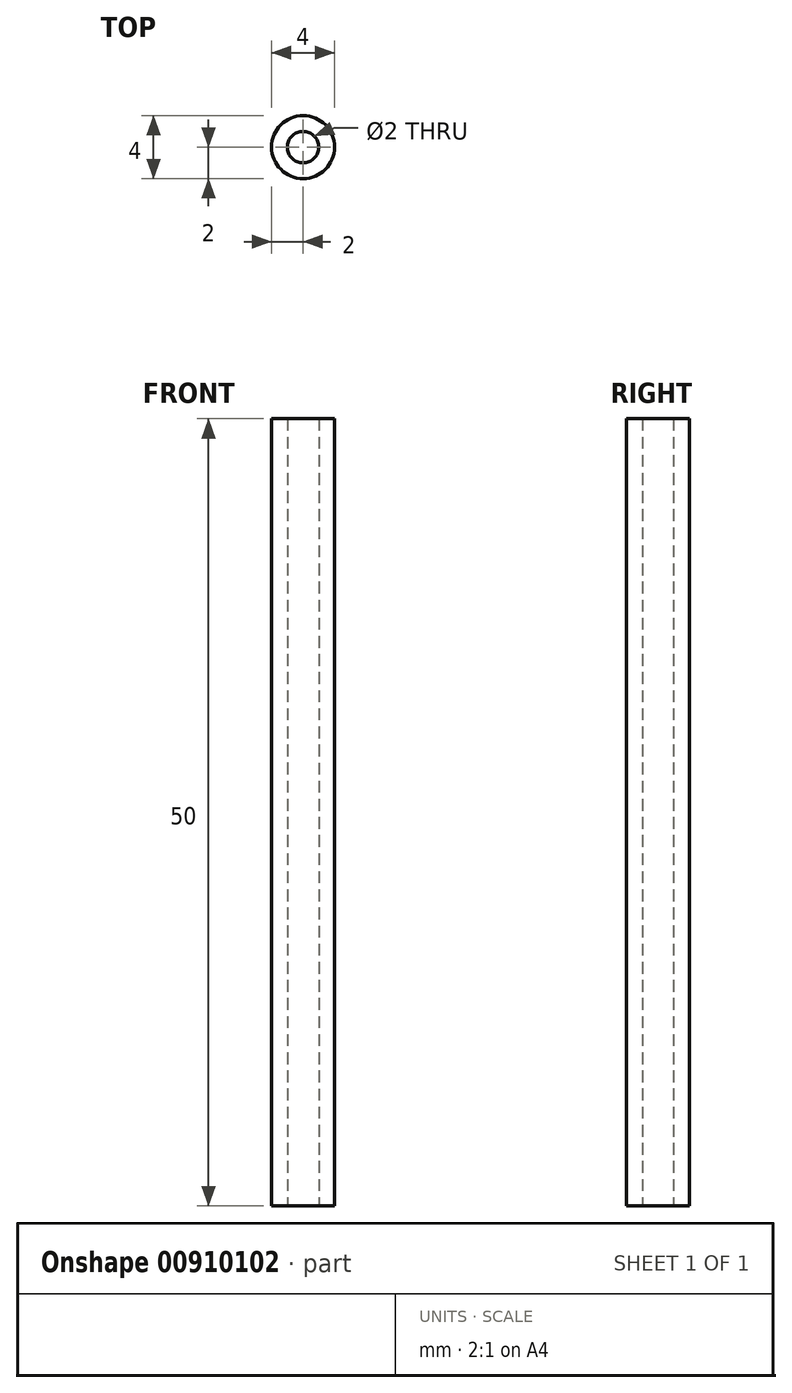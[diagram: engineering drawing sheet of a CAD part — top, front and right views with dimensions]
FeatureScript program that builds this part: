
annotation { "Feature Type Name" : "Feature", "Feature Type Description" : "" }
export const myFeature = defineFeature(function(context is Context, id is Id, definition is map)
    precondition{}
    {
        {
            var Q0;
            Q0=qCreatedBy(makeId("Top.planeOp"),FACE);
            var sketch = newSketch(context, id + "F0", { "sketchPlane" : qUnion([Q0])});
            skCircle(sketch, "E0", {"center": v(0, 0) * mm, "radius": 2 * mm});
            skCircle(sketch, "E1", {"center": v(0, 0) * mm, "radius": 1 * mm});
            skSolve(sketch);
        }
        {
            var Q0;
            Q0=makeQuery(id+"F0.imprint","IMPRINT",FACE,{"disambiguationData":[TD([[makeQuery(id+"F0.imprint","IMPRINT",EDGE,{"derivedFrom":sQuery(id+"F0.wireOp",EDGE,"E0")}),1.0]])]});
            extrude(context, id + "F1", {"entities" : qUnion([Q0]), "depth" : 50 * mm, "offsetDistance" : 25 * mm});
        }
    });
